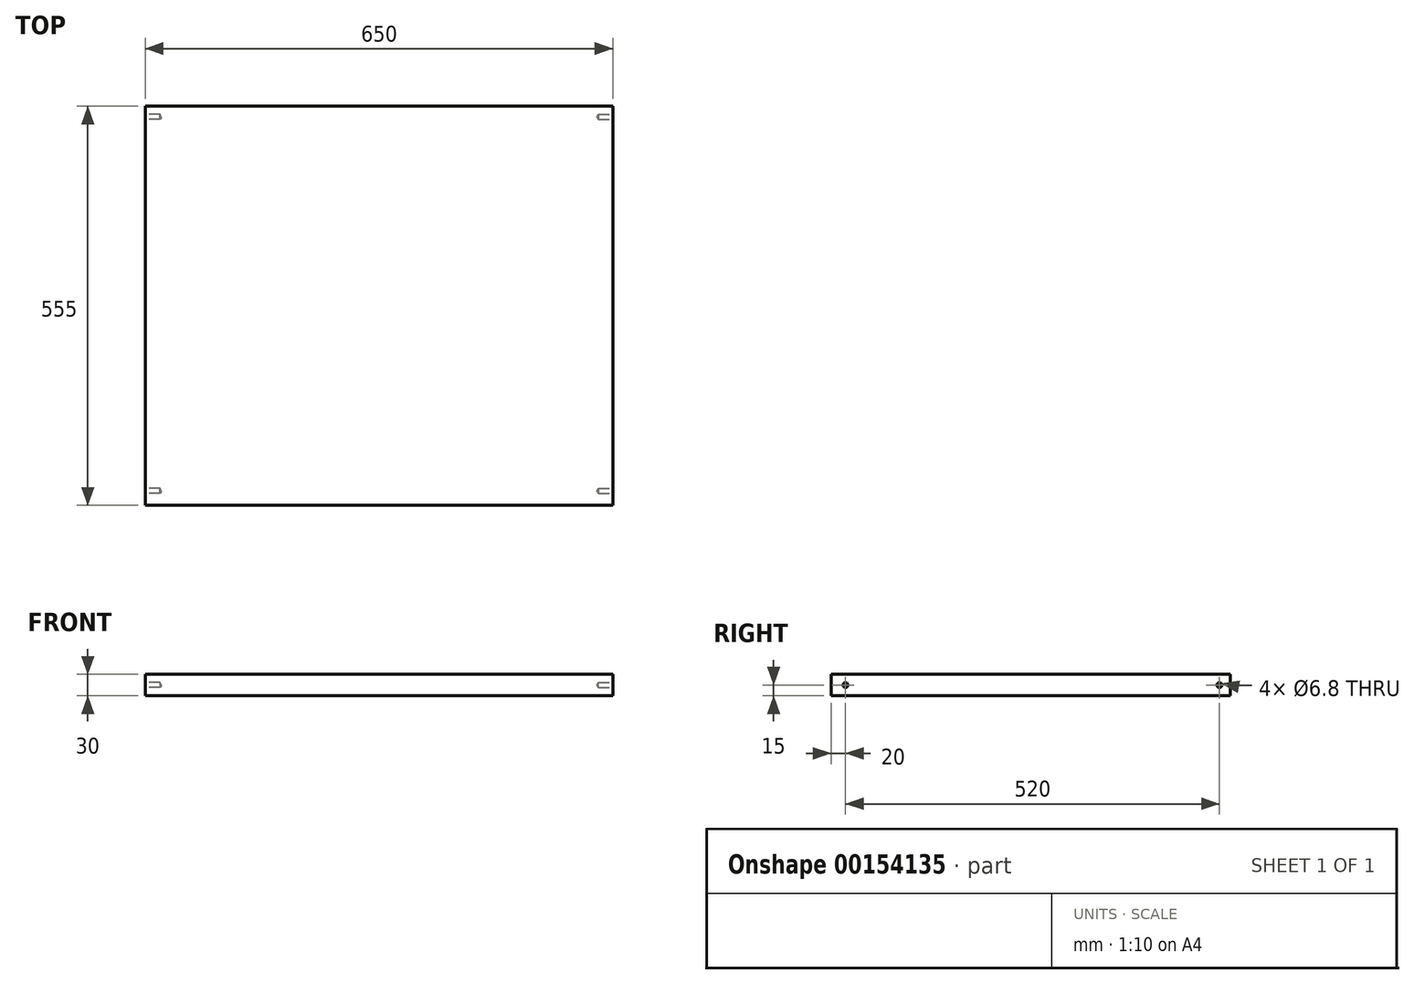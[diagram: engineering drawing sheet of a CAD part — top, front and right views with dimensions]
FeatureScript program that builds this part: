
annotation { "Feature Type Name" : "Feature", "Feature Type Description" : "" }
export const myFeature = defineFeature(function(context is Context, id is Id, definition is map)
    precondition{}
    {
        {
            var Q0;
            Q0=qCreatedBy(makeId("Top.planeOp"),FACE);
            var sketch = newSketch(context, id + "F0", { "sketchPlane" : qUnion([Q0])});
            skLineSegment(sketch, "E0.bottom", {"start": v(325, -277.5) * mm, "end": v(-325, -277.5) * mm});
            skLineSegment(sketch, "E0.top", {"start": v(325, 277.5) * mm, "end": v(-325, 277.5) * mm});
            skLineSegment(sketch, "E0.left", {"start": v(325, -277.5) * mm, "end": v(325, 277.5) * mm});
            skLineSegment(sketch, "E0.right", {"start": v(-325, -277.5) * mm, "end": v(-325, 277.5) * mm});
            skPoint(sketch, "E0.middle", {"position": v(0, 0) * mm});
            skSolve(sketch);
        }
        {
            var Q0;
            Q0=qSketchRegion(id+"F0",true);
            extrude(context, id + "F1", {"entities" : qUnion([Q0]), "depth" : 30 * mm});
        }
        {
            var Q0;
            Q0=makeQuery(id+"F1.opExtrude","SWEPT_FACE",FACE,{"disambiguationData":[OSD([sQuery(id+"F0.wireOp",EDGE,"E0.right")])]});
            var sketch = newSketch(context, id + "F2", { "sketchPlane" : qUnion([Q0])});
            skLineSegment(sketch, "E1.bottom", {"start": v(-277.5, 0) * mm, "end": v(277.5, 0) * mm});
            skLineSegment(sketch, "E1.top", {"start": v(-277.5, 30) * mm, "end": v(277.5, 30) * mm});
            skLineSegment(sketch, "E1.left", {"start": v(-277.5, 0) * mm, "end": v(-277.5, 30) * mm});
            skLineSegment(sketch, "E1.right", {"start": v(277.5, 0) * mm, "end": v(277.5, 30) * mm});
            skPoint(sketch, "E2", {"position": v(-262.5, 15) * mm});
            skPoint(sketch, "E3", {"position": v(257.5, 15) * mm});
            skSolve(sketch);
        }
        {
            var Q0;
            Q0=makeQuery(id+"F1.opExtrude","SWEPT_FACE",FACE,{"disambiguationData":[OSD([sQuery(id+"F0.wireOp",EDGE,"E0.left")])]});
            var sketch = newSketch(context, id + "F3", { "sketchPlane" : qUnion([Q0])});
            skLineSegment(sketch, "E4.bottom", {"start": v(-277.5, 0) * mm, "end": v(277.5, 0) * mm});
            skLineSegment(sketch, "E4.top", {"start": v(-277.5, 30) * mm, "end": v(277.5, 30) * mm});
            skLineSegment(sketch, "E4.left", {"start": v(-277.5, 0) * mm, "end": v(-277.5, 30) * mm});
            skLineSegment(sketch, "E4.right", {"start": v(277.5, 0) * mm, "end": v(277.5, 30) * mm});
            skPoint(sketch, "E5", {"position": v(-257.5, 15) * mm});
            skPoint(sketch, "E6", {"position": v(262.5, 15) * mm});
            skSolve(sketch);
        }
        {
            var Q0;
            Q0=sQuery(id+"F2.wireOp",VERTEX,"E3");
            var Q1;
            Q1=sQuery(id+"F2.wireOp",VERTEX,"E2");
            var Q2;
            Q2=sQuery(id+"F3.wireOp",VERTEX,"E6");
            var Q3;
            Q3=sQuery(id+"F3.wireOp",VERTEX,"E5");
            var Q4;
            Q4=makeQuery(id+"F1.opExtrude","SWEPT_BODY",BODY,{"disambiguationData":[OSD([sQuery(id+"F0.wireOp",EDGE,"E0.bottom"),sQuery(id+"F0.wireOp",EDGE,"E0.top"),sQuery(id+"F0.wireOp",EDGE,"E0.left"),sQuery(id+"F0.wireOp",EDGE,"E0.right")])]});
            hole(context, id + "F4", {"style" : HoleStyle.SIMPLE, "endStyle" : HoleEndStyle.BLIND, "standardTappedOrClearance" : lookupTablePath({ "standard" : "ISO", "engagement" : "75%", "pitch" : "1.25 mm", "size" : "M8", "type" : "Tapped" }), "standardBlindInLast" : lookupTablePath({ "standard" : "ISO", "engagement" : "75%", "pitch" : "1.25 mm", "size" : "M8", "type" : "Tapped" }), "holeDiameter" : 6.8 * mm, "holeDepth" : 20 * mm, "locations" : qUnion([Q0, Q1, Q2, Q3]), "scope" : qUnion([Q4]), "majorDiameter" : 8 * mm});
        }
    });
